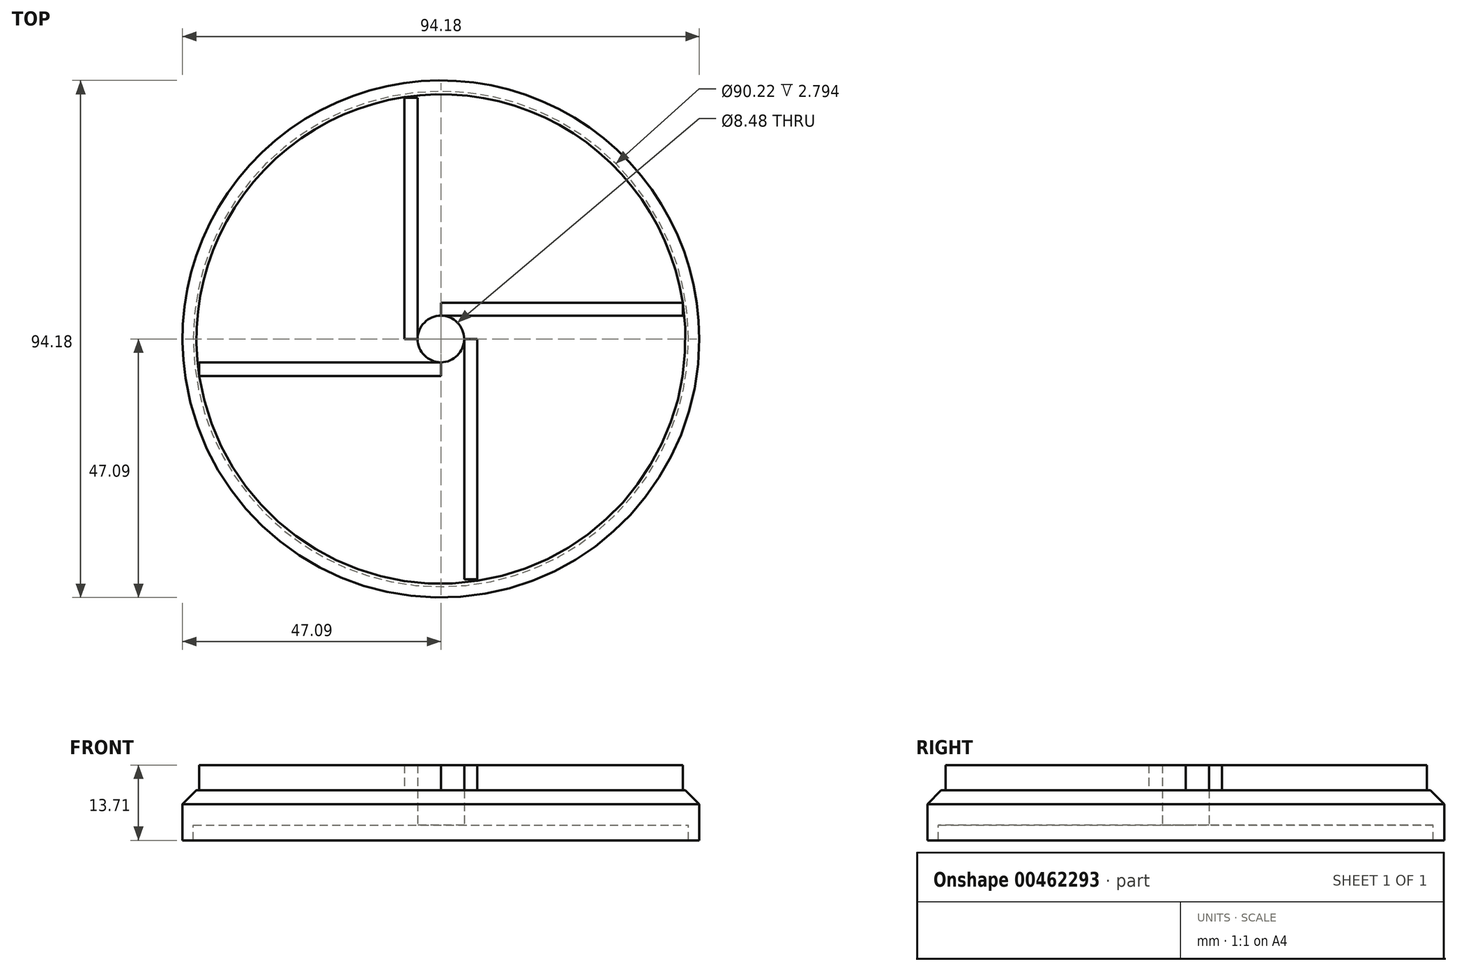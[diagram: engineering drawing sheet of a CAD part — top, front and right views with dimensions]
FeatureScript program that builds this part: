
annotation { "Feature Type Name" : "Feature", "Feature Type Description" : "" }
export const myFeature = defineFeature(function(context is Context, id is Id, definition is map)
    precondition{}
    {
        {
            var Q0;
            Q0=qCreatedBy(makeId("Top.planeOp"),FACE);
            var sketch = newSketch(context, id + "F0", { "sketchPlane" : qUnion([Q0])});
            skCircle(sketch, "E0", {"center": v(0, 0) * mm, "radius": 47.09 * mm});
            skCircle(sketch, "E1", {"center": v(0, 0) * mm, "radius": 10.94 * mm});
            skCircle(sketch, "E2", {"center": v(0, 0) * mm, "radius": 4.24 * mm});
            skCircle(sketch, "E3", {"center": v(0, 0) * mm, "radius": 45.11 * mm});
            skSolve(sketch);
        }
        {
            var Q0;
            Q0=makeQuery(id+"F0.imprint","IMPRINT",FACE,{"disambiguationData":[TD([[makeQuery(id+"F0.imprint","IMPRINT",EDGE,{"derivedFrom":sQuery(id+"F0.wireOp",EDGE,"E1")}),-1.0]])]});
            var Q1;
            Q1=makeQuery(id+"F0.imprint","IMPRINT",FACE,{"disambiguationData":[TD([[makeQuery(id+"F0.imprint","IMPRINT",EDGE,{"derivedFrom":sQuery(id+"F0.wireOp",EDGE,"E0")}),1.0]])]});
            var Q2;
            Q2=makeQuery(id+"F0.imprint","IMPRINT",FACE,{"disambiguationData":[TD([[makeQuery(id+"F0.imprint","IMPRINT",EDGE,{"derivedFrom":sQuery(id+"F0.wireOp",EDGE,"E1")}),1.0]])]});
            extrude(context, id + "F1", {"entities" : qUnion([Q0, Q1, Q2]), "depth" : 3.8 * mm});
        }
        {
            var Q0;
            Q0=makeQuery(id+"F1.opExtrude","CAP_EDGE",EDGE,{"disambiguationData":[OSD([sQuery(id+"F0.wireOp",EDGE,"E0")])],"isStart":false});
            chamfer(context, id + "F2", {"entities" : qUnion([Q0]), "width" : 2.54 * mm, "tangentPropagation" : true});
        }
        {
            var Q0;
            Q0=makeQuery(id+"F1.opExtrude","CAP_FACE",FACE,{"disambiguationData":[OSD([sQuery(id+"F0.wireOp",EDGE,"E0"),sQuery(id+"F0.wireOp",EDGE,"E2")])],"isStart":true});
            var sketch = newSketch(context, id + "F3", { "sketchPlane" : qUnion([Q0])});
            skCircle(sketch, "E4", {"center": v(0, 0) * mm, "radius": 47.09 * mm});
            skCircle(sketch, "E5", {"center": v(0, 0) * mm, "radius": 10.94 * mm});
            skCircle(sketch, "E6", {"center": v(0, 0) * mm, "radius": 4.24 * mm});
            skCircle(sketch, "E7", {"center": v(0, 0) * mm, "radius": 45.11 * mm});
            skSolve(sketch);
        }
        {
            var Q0;
            Q0=makeQuery(id+"F3.imprint","IMPRINT",FACE,{"disambiguationData":[TD([[makeQuery(id+"F3.imprint","IMPRINT",EDGE,{"derivedFrom":sQuery(id+"F3.wireOp",EDGE,"E4")}),-1.0]])]});
            extrude(context, id + "F4", {"entities" : qUnion([Q0]), "operationType" : NewBodyOperationType.ADD, "depth" : 5.33 * mm});
        }
        {
            var Q0;
            Q0=makeQuery(id+"F1.opExtrude","CAP_FACE",FACE,{"disambiguationData":[OSD([sQuery(id+"F0.wireOp",EDGE,"E0"),sQuery(id+"F0.wireOp",EDGE,"E2")])],"isStart":false});
            var sketch = newSketch(context, id + "F5", { "sketchPlane" : qUnion([Q0])});
            skLineSegment(sketch, "E8.bottom", {"start": v(4.24, 0) * mm, "end": v(6.62, 0) * mm});
            skLineSegment(sketch, "E8.top", {"start": v(4.24, -43.77) * mm, "end": v(6.62, -43.77) * mm});
            skLineSegment(sketch, "E8.left", {"start": v(4.24, 0) * mm, "end": v(4.24, -43.77) * mm});
            skLineSegment(sketch, "E8.right", {"start": v(6.62, 0) * mm, "end": v(6.62, -43.77) * mm});
            skLineSegment(sketch, "E9.bottom", {"start": v(0, 4.24) * mm, "end": v(44.06, 4.24) * mm});
            skLineSegment(sketch, "E9.top", {"start": v(0, 6.6) * mm, "end": v(44.06, 6.6) * mm});
            skLineSegment(sketch, "E9.left", {"start": v(0, 4.24) * mm, "end": v(0, 6.6) * mm});
            skLineSegment(sketch, "E9.right", {"start": v(44.06, 4.24) * mm, "end": v(44.06, 6.6) * mm});
            skLineSegment(sketch, "E10.bottom", {"start": v(-4.24, 0) * mm, "end": v(-6.68, 0) * mm});
            skLineSegment(sketch, "E10.top", {"start": v(-4.24, 43.93) * mm, "end": v(-6.68, 43.93) * mm});
            skLineSegment(sketch, "E10.left", {"start": v(-4.24, 0) * mm, "end": v(-4.24, 43.93) * mm});
            skLineSegment(sketch, "E10.right", {"start": v(-6.68, 0) * mm, "end": v(-6.68, 43.93) * mm});
            skPoint(sketch, "E11.firstSnap0", {"position": v(0, 5.42) * mm});
            skLineSegment(sketch, "E11.bottom", {"start": v(0, -4.24) * mm, "end": v(-44.04, -4.24) * mm});
            skLineSegment(sketch, "E11.top", {"start": v(0, -6.74) * mm, "end": v(-44.04, -6.74) * mm});
            skLineSegment(sketch, "E11.left", {"start": v(0, -4.24) * mm, "end": v(0, -6.74) * mm});
            skLineSegment(sketch, "E11.right", {"start": v(-44.04, -4.24) * mm, "end": v(-44.04, -6.74) * mm});
            skSolve(sketch);
        }
        {
            var Q0;
            Q0=makeQuery(id+"F1.opExtrude","CAP_FACE",FACE,{"disambiguationData":[OSD([sQuery(id+"F0.wireOp",EDGE,"E0"),sQuery(id+"F0.wireOp",EDGE,"E2")])],"isStart":true});
            extrude(context, id + "F6", {"entities" : qUnion([Q0]), "operationType" : NewBodyOperationType.ADD, "depth" : 2.54 * mm});
        }
        {
            var Q0;
            Q0=makeQuery(id+"F5.imprint","IMPRINT",FACE,{"disambiguationData":[TD([[makeQuery(id+"F5.imprint","IMPRINT",EDGE,{"derivedFrom":sQuery(id+"F5.wireOp",EDGE,"E10.bottom")}),-1.0]])]});
            var Q1;
            Q1=makeQuery(id+"F5.imprint","IMPRINT",FACE,{"disambiguationData":[TD([[makeQuery(id+"F5.imprint","IMPRINT",EDGE,{"derivedFrom":sQuery(id+"F5.wireOp",EDGE,"E9.bottom")}),1.0]])]});
            var Q2;
            Q2=makeQuery(id+"F5.imprint","IMPRINT",FACE,{"disambiguationData":[TD([[makeQuery(id+"F5.imprint","IMPRINT",EDGE,{"derivedFrom":sQuery(id+"F5.wireOp",EDGE,"E8.bottom")}),-1.0]])]});
            var Q3;
            Q3=makeQuery(id+"F5.imprint","IMPRINT",FACE,{"disambiguationData":[TD([[makeQuery(id+"F5.imprint","IMPRINT",EDGE,{"derivedFrom":sQuery(id+"F5.wireOp",EDGE,"E11.bottom")}),1.0]])]});
            extrude(context, id + "F7", {"entities" : qUnion([Q0, Q1, Q2, Q3]), "operationType" : NewBodyOperationType.ADD, "depth" : 4.57 * mm});
        }
    });
